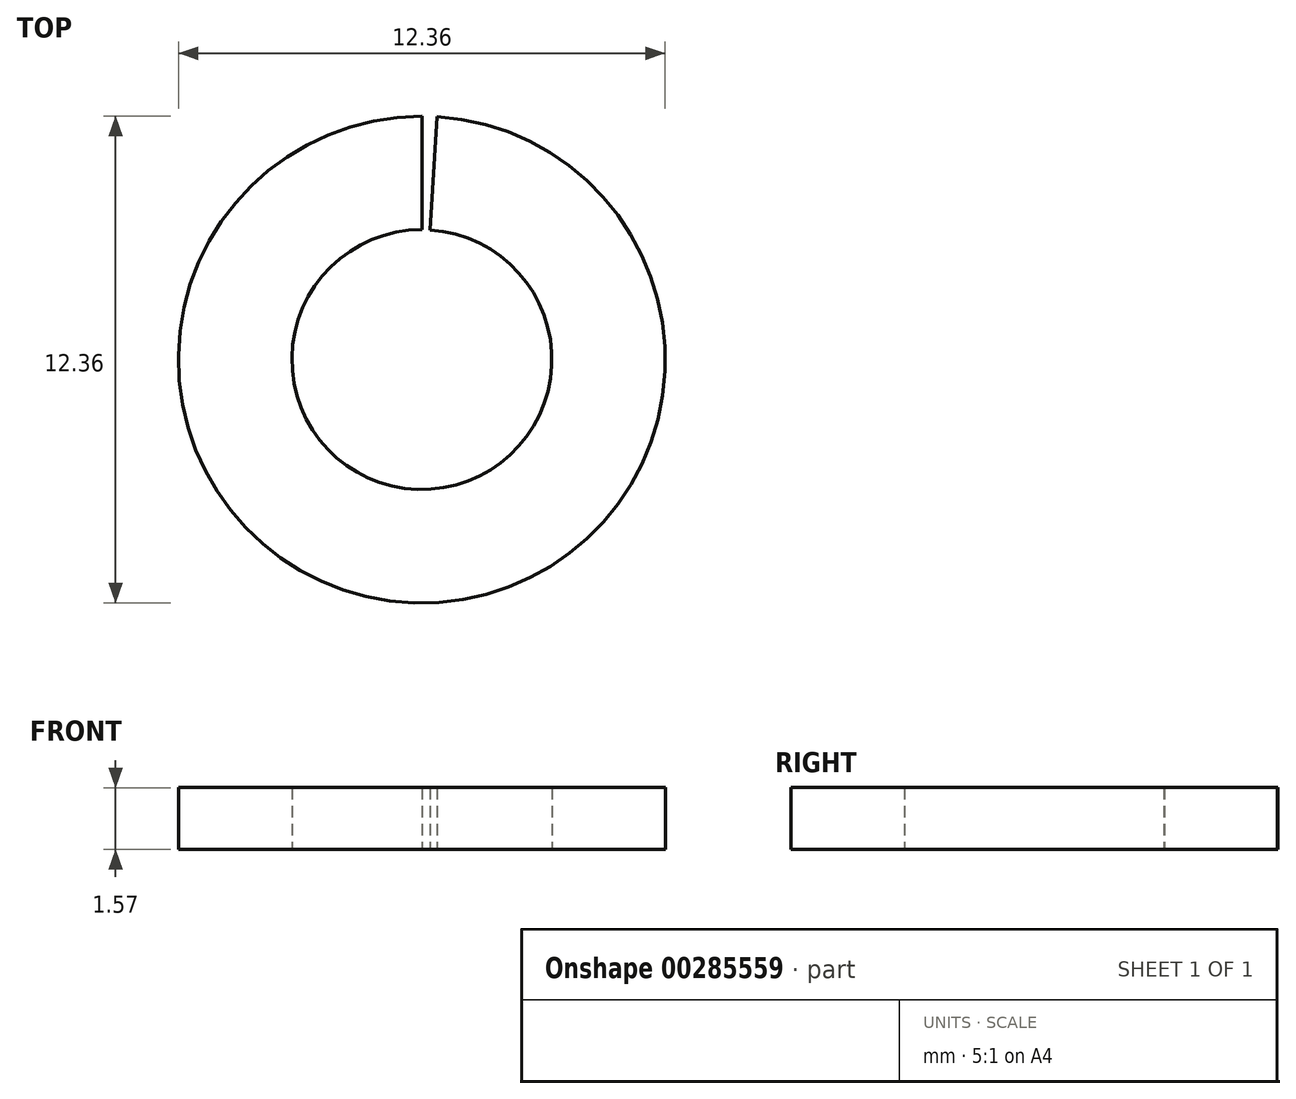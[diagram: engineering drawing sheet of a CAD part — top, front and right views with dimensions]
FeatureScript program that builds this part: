
annotation { "Feature Type Name" : "Feature", "Feature Type Description" : "" }
export const myFeature = defineFeature(function(context is Context, id is Id, definition is map)
    precondition{}
    {
        {
            var Q0;
            Q0=qCreatedBy(makeId("Top.planeOp"),FACE);
            var sketch = newSketch(context, id + "F0", { "sketchPlane" : qUnion([Q0])});
            skArc(sketch, "E0", {"start": v(0, 3.3) * mm, "mid": v(-0.1, -3.3) * mm, "end": v(0.2, 3.3) * mm});
            skArc(sketch, "E1", {"start": v(0, 6.18) * mm, "mid": v(-0.2, -6.18) * mm, "end": v(0.39, 6.17) * mm});
            skFitSpline(sketch, "E2.0", {"points": [v(0.2, 3.3) * mm, v(0.27, 4.25) * mm, v(0.33, 5.21) * mm, v(0.39, 6.17) * mm]});
            skFitSpline(sketch, "E3.0", {"points": [v(0, 6.18) * mm, v(0, 5.22) * mm, v(0, 4.26) * mm, v(0, 3.3) * mm]});
            skSolve(sketch);
        }
        {
            var Q0;
            Q0=makeQuery(id+"F0.imprint","IMPRINT",FACE,{"disambiguationData":[TD([[makeQuery(id+"F0.imprint","IMPRINT",EDGE,{"derivedFrom":sQuery(id+"F0.wireOp",EDGE,"E0")}),-1.0]])]});
            extrude(context, id + "F1", {"entities" : qUnion([Q0]), "depth" : 1.57 * mm});
        }
    });
